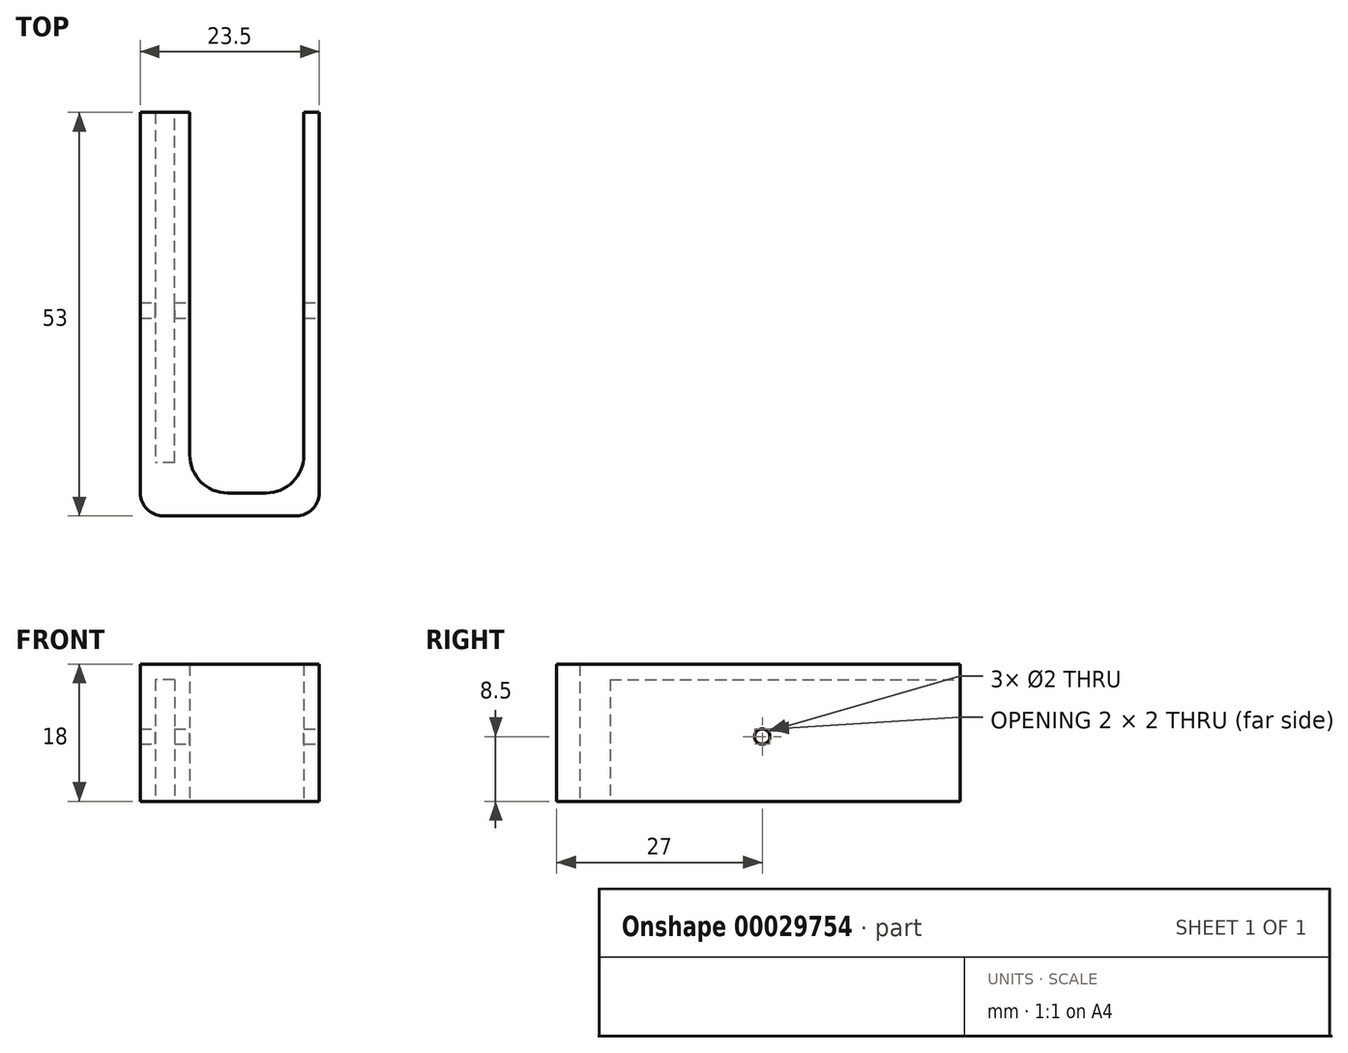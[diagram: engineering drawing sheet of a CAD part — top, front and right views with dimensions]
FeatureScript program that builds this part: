
annotation { "Feature Type Name" : "Feature", "Feature Type Description" : "" }
export const myFeature = defineFeature(function(context is Context, id is Id, definition is map)
    precondition{}
    {
        {
            var Q0;
            Q0=qCreatedBy(makeId("Top.planeOp"),FACE);
            var sketch = newSketch(context, id + "F0", { "sketchPlane" : qUnion([Q0])});
            skLineSegment(sketch, "E0.top", {"start": v(0, 53) * mm, "end": v(-2, 53) * mm});
            skLineSegment(sketch, "E0.left", {"start": v(0, 0) * mm, "end": v(0, 53) * mm});
            skLineSegment(sketch, "E0.right", {"start": v(-19, 7) * mm, "end": v(-19, 53) * mm});
            skLineSegment(sketch, "E1.top", {"start": v(-17, 3) * mm, "end": v(-2, 3) * mm});
            skLineSegment(sketch, "E1.left", {"start": v(-17, 53) * mm, "end": v(-17, 3) * mm});
            skLineSegment(sketch, "E1.right", {"start": v(-2, 53) * mm, "end": v(-2, 3) * mm});
            skLineSegment(sketch, "E2.trimOffspring", {"start": v(-17, 53) * mm, "end": v(-19, 53) * mm});
            skLineSegment(sketch, "E3", {"start": v(-19, 0) * mm, "end": v(0, 0) * mm});
            skPoint(sketch, "E4.end.orphan", {"position": v(12, 0) * mm});
            skPoint(sketch, "E5.end.orphan", {"position": v(-31, 0) * mm});
            skLineSegment(sketch, "E6", {"start": v(-19, 0) * mm, "end": v(-23.5, 0) * mm});
            skLineSegment(sketch, "E7", {"start": v(-23.5, 0) * mm, "end": v(-23.5, 53) * mm});
            skLineSegment(sketch, "E8", {"start": v(-23.5, 53) * mm, "end": v(-21.5, 53) * mm});
            skLineSegment(sketch, "E9", {"start": v(-21.5, 53) * mm, "end": v(-21.5, 7) * mm});
            skLineSegment(sketch, "E10", {"start": v(-19, 7) * mm, "end": v(-21.5, 7) * mm});
            skPoint(sketch, "E11.orphan", {"position": v(-21.5, 3) * mm});
            skSolve(sketch);
        }
        {
            var Q0;
            Q0=makeQuery(id+"F0.imprint","IMPRINT",FACE,{"disambiguationData":[TD([[makeQuery(id+"F0.imprint","IMPRINT",EDGE,{"derivedFrom":sQuery(id+"F0.wireOp",EDGE,"E0.top")}),1.0]])]});
            extrude(context, id + "F1", {"entities" : qUnion([Q0]), "depth" : 16 * mm});
        }
        {
            var Q0;
            Q0=makeQuery(id+"F1.opExtrude","SWEPT_FACE",FACE,{"disambiguationData":[OSD([sQuery(id+"F0.wireOp",EDGE,"E0.left")])]});
            var sketch = newSketch(context, id + "F2", { "sketchPlane" : qUnion([Q0])});
            skCircle(sketch, "E12", {"center": v(27, 8.5) * mm, "radius": 1 * mm});
            skSolve(sketch);
        }
        {
            var Q0;
            Q0=qSketchRegion(id+"F2",true);
            extrude(context, id + "F3", {"entities" : qUnion([Q0]), "operationType" : NewBodyOperationType.REMOVE, "oppositeDirection" : true, "depth" : 25 * mm});
        }
        {
            var Q0;
            Q0=makeQuery(id+"F1.opExtrude","SWEPT_EDGE",EDGE,{"disambiguationData":[OSD([sQuery(id+"F0.wireOp",EDGE,"E1.top"),sQuery(id+"F0.wireOp",EDGE,"E1.right")])]});
            var Q1;
            Q1=makeQuery(id+"F1.opExtrude","SWEPT_EDGE",EDGE,{"disambiguationData":[OSD([sQuery(id+"F0.wireOp",EDGE,"E1.top"),sQuery(id+"F0.wireOp",EDGE,"E1.left")])]});
            fillet(context, id + "F4", {"entities" : qUnion([Q0, Q1]), "radius" : 5 * mm, "tangentPropagation" : true, "allowEdgeOverflow" : false});
        }
        {
            var Q0;
            Q0=makeQuery(id+"F1.opExtrude","SWEPT_EDGE",EDGE,{"disambiguationData":[OSD([sQuery(id+"F0.wireOp",EDGE,"E0.left"),sQuery(id+"F0.wireOp",EDGE,"E3")])]});
            var Q1;
            Q1=makeQuery(id+"F1.opExtrude","SWEPT_EDGE",EDGE,{"disambiguationData":[OSD([sQuery(id+"F0.wireOp",EDGE,"E6"),sQuery(id+"F0.wireOp",EDGE,"E7")])]});
            fillet(context, id + "F5", {"entities" : qUnion([Q0, Q1]), "radius" : 3 * mm, "tangentPropagation" : true, "allowEdgeOverflow" : false});
        }
        {
            var Q0;
            Q0=makeQuery(id+"F1.opExtrude","CAP_FACE",FACE,{"disambiguationData":[OSD([sQuery(id+"F0.wireOp",EDGE,"E0.top"),sQuery(id+"F0.wireOp",EDGE,"E0.left"),sQuery(id+"F0.wireOp",EDGE,"E0.right"),sQuery(id+"F0.wireOp",EDGE,"E1.top"),sQuery(id+"F0.wireOp",EDGE,"E1.left"),sQuery(id+"F0.wireOp",EDGE,"E1.right"),sQuery(id+"F0.wireOp",EDGE,"E2.trimOffspring"),sQuery(id+"F0.wireOp",EDGE,"E3"),sQuery(id+"F0.wireOp",EDGE,"E6"),sQuery(id+"F0.wireOp",EDGE,"E7"),sQuery(id+"F0.wireOp",EDGE,"E8"),sQuery(id+"F0.wireOp",EDGE,"E9"),sQuery(id+"F0.wireOp",EDGE,"E10")])],"isStart":false});
            var sketch = newSketch(context, id + "F6", { "sketchPlane" : qUnion([Q0])});
            skLineSegment(sketch, "E13", {"start": v(-19, 53) * mm, "end": v(-21.5, 53) * mm});
            skLineSegment(sketch, "E14.0", {"start": v(-19, 7) * mm, "end": v(-19, 53) * mm});
            skLineSegment(sketch, "E15.0", {"start": v(-21.5, 53) * mm, "end": v(-21.5, 7) * mm});
            skLineSegment(sketch, "E16.0", {"start": v(-19, 7) * mm, "end": v(-21.5, 7) * mm});
            skSolve(sketch);
        }
        {
            var Q0;
            {var subQ12=sQuery(id+"F0.wireOp",EDGE,"E0.top");Q0=makeQuery(id+"F6.imprint","IMPRINT",FACE,{"disambiguationData":[TD([[makeQuery(id+"F6.imprint","IMPRINT",EDGE,{"derivedFrom":makeQuery(id+"F1.opExtrude","CAP_EDGE",EDGE,{"disambiguationData":[OSD([subQ12])],"isStart":false})}),1.0]])]});}
            extrude(context, id + "F7", {"entities" : qUnion([Q0]), "operationType" : NewBodyOperationType.ADD, "depth" : 2 * mm});
        }
        {
            var Q0;
            Q0 = qSketchRegion(id + "F6", true);
            extrude(context, id + "F8", {"entities" : qUnion([Q0]), "operationType" : NewBodyOperationType.ADD, "depth" : 2 * mm});
        }
    });
